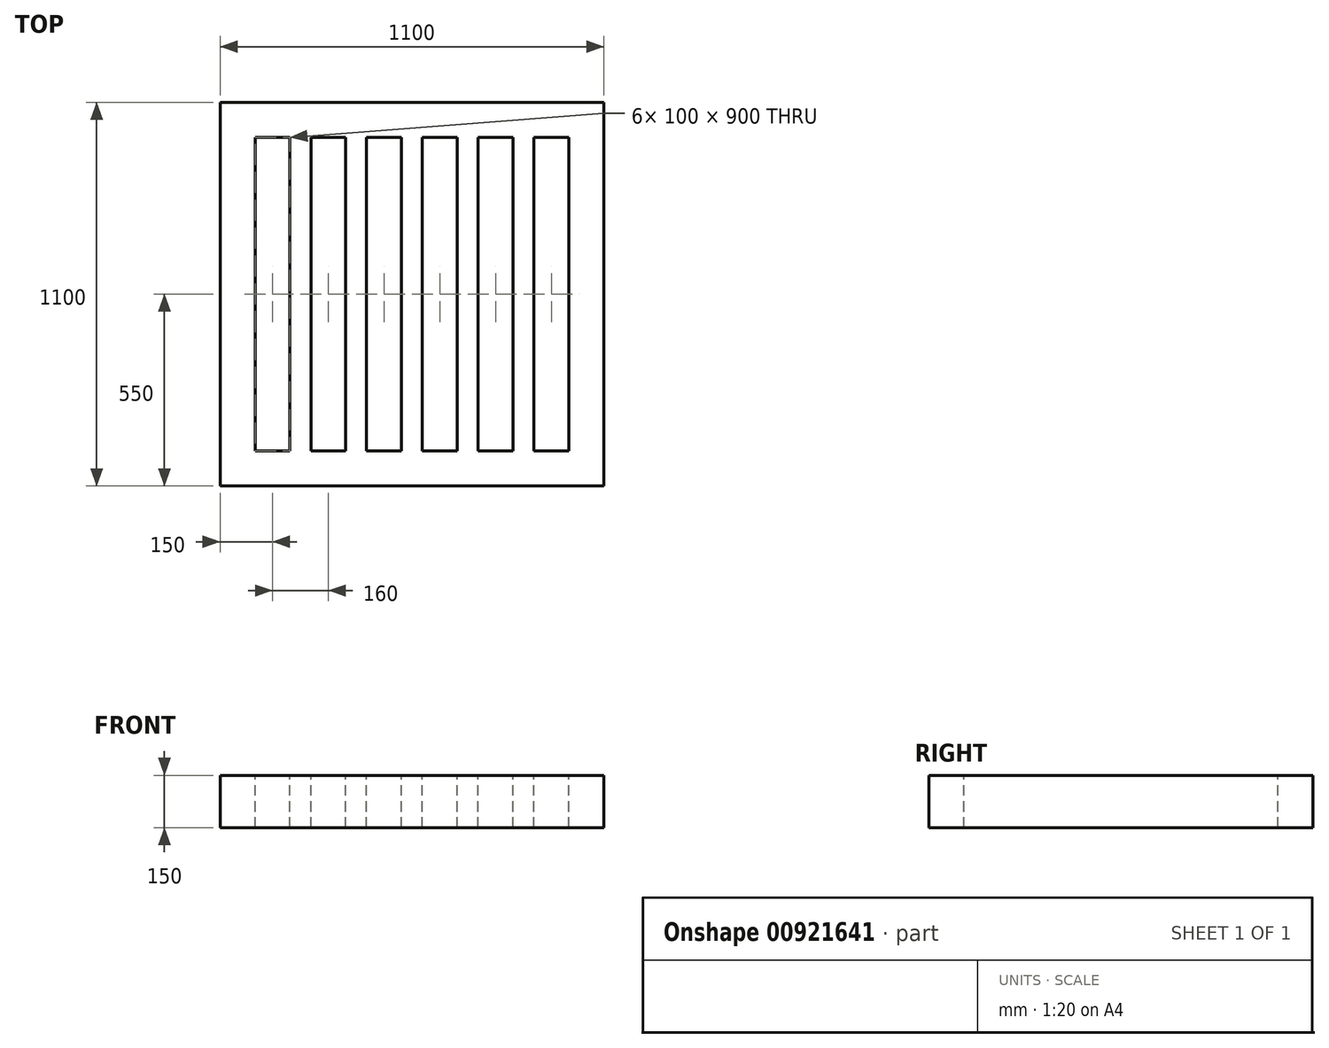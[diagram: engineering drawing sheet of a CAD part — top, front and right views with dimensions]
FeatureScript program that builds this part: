
annotation { "Feature Type Name" : "Feature", "Feature Type Description" : "" }
export const myFeature = defineFeature(function(context is Context, id is Id, definition is map)
    precondition{}
    {
        {
            var Q0;
            Q0=qCreatedBy(makeId("Top.planeOp"),FACE);
            var sketch = newSketch(context, id + "F0", { "sketchPlane" : qUnion([Q0])});
            skLineSegment(sketch, "E0.bottom", {"start": v(550, 550) * mm, "end": v(-550, 550) * mm});
            skLineSegment(sketch, "E0.top", {"start": v(550, -550) * mm, "end": v(-550, -550) * mm});
            skLineSegment(sketch, "E0.left", {"start": v(550, 550) * mm, "end": v(550, -550) * mm});
            skLineSegment(sketch, "E0.right", {"start": v(-550, 550) * mm, "end": v(-550, -550) * mm});
            skPoint(sketch, "E0.middle", {"position": v(0, 0) * mm});
            skSolve(sketch);
        }
        {
            var Q0;
            Q0=makeQuery(id+"F0.imprint","IMPRINT",FACE,{"disambiguationData":[TD([[makeQuery(id+"F0.imprint","IMPRINT",EDGE,{"derivedFrom":sQuery(id+"F0.wireOp",EDGE,"E0.bottom")}),1.0]])]});
            extrude(context, id + "F1", {"entities" : qUnion([Q0]), "depth" : 150 * mm, "offsetDistance" : 25 * mm});
        }
        {
            var Q0;
            Q0=makeQuery(id+"F1.opExtrude","CAP_FACE",FACE,{"disambiguationData":[OSD([sQuery(id+"F0.wireOp",EDGE,"E0.bottom"),sQuery(id+"F0.wireOp",EDGE,"E0.top"),sQuery(id+"F0.wireOp",EDGE,"E0.left"),sQuery(id+"F0.wireOp",EDGE,"E0.right")])],"isStart":false});
            var sketch = newSketch(context, id + "F2", { "sketchPlane" : qUnion([Q0])});
            skLineSegment(sketch, "E1.bottom", {"start": v(-450, 450) * mm, "end": v(-350, 450) * mm});
            skLineSegment(sketch, "E1.top", {"start": v(-450, -450) * mm, "end": v(-350, -450) * mm});
            skLineSegment(sketch, "E1.left", {"start": v(-450, 450) * mm, "end": v(-450, -450) * mm});
            skLineSegment(sketch, "E1.right", {"start": v(-350, 450) * mm, "end": v(-350, -450) * mm});
            skLineSegment(sketch, "E2.1.0.0", {"start": v(-290, 450) * mm, "end": v(-190, 450) * mm});
            skLineSegment(sketch, "E2.1.0.1", {"start": v(-190, 450) * mm, "end": v(-190, -450) * mm});
            skLineSegment(sketch, "E2.1.0.2", {"start": v(-290, 450) * mm, "end": v(-290, -450) * mm});
            skLineSegment(sketch, "E2.1.0.3", {"start": v(-290, -450) * mm, "end": v(-190, -450) * mm});
            skLineSegment(sketch, "E2.2.0.0", {"start": v(-130, 450) * mm, "end": v(-30, 450) * mm});
            skLineSegment(sketch, "E2.2.0.1", {"start": v(-30, 450) * mm, "end": v(-30, -450) * mm});
            skLineSegment(sketch, "E2.2.0.2", {"start": v(-130, 450) * mm, "end": v(-130, -450) * mm});
            skLineSegment(sketch, "E2.2.0.3", {"start": v(-130, -450) * mm, "end": v(-30, -450) * mm});
            skLineSegment(sketch, "E2.3.0.0", {"start": v(30, 450) * mm, "end": v(130, 450) * mm});
            skLineSegment(sketch, "E2.3.0.1", {"start": v(130, 450) * mm, "end": v(130, -450) * mm});
            skLineSegment(sketch, "E2.3.0.2", {"start": v(30, 450) * mm, "end": v(30, -450) * mm});
            skLineSegment(sketch, "E2.3.0.3", {"start": v(30, -450) * mm, "end": v(130, -450) * mm});
            skLineSegment(sketch, "E2.4.0.0", {"start": v(190, 450) * mm, "end": v(290, 450) * mm});
            skLineSegment(sketch, "E2.4.0.1", {"start": v(290, 450) * mm, "end": v(290, -450) * mm});
            skLineSegment(sketch, "E2.4.0.2", {"start": v(190, 450) * mm, "end": v(190, -450) * mm});
            skLineSegment(sketch, "E2.4.0.3", {"start": v(190, -450) * mm, "end": v(290, -450) * mm});
            skLineSegment(sketch, "E2.5.0.0", {"start": v(350, 450) * mm, "end": v(450, 450) * mm});
            skLineSegment(sketch, "E2.5.0.1", {"start": v(450, 450) * mm, "end": v(450, -450) * mm});
            skLineSegment(sketch, "E2.5.0.2", {"start": v(350, 450) * mm, "end": v(350, -450) * mm});
            skLineSegment(sketch, "E2.5.0.3", {"start": v(350, -450) * mm, "end": v(450, -450) * mm});
            skLineSegment(sketch, "E2.direction1", {"start": v(-450, 450) * mm, "end": v(-290, 450) * mm, "construction": true});
            skSolve(sketch);
        }
        {
            var Q0;
            Q0=makeQuery(id+"F2.imprint","IMPRINT",FACE,{"disambiguationData":[TD([[makeQuery(id+"F2.imprint","IMPRINT",EDGE,{"derivedFrom":sQuery(id+"F2.wireOp",EDGE,"E1.bottom")}),-1.0]])]});
            var Q1;
            Q1=makeQuery(id+"F2.imprint","IMPRINT",FACE,{"disambiguationData":[TD([[makeQuery(id+"F2.imprint","IMPRINT",EDGE,{"derivedFrom":sQuery(id+"F2.wireOp",EDGE,"E2.1.0.0")}),-1.0]])]});
            var Q2;
            Q2=makeQuery(id+"F2.imprint","IMPRINT",FACE,{"disambiguationData":[TD([[makeQuery(id+"F2.imprint","IMPRINT",EDGE,{"derivedFrom":sQuery(id+"F2.wireOp",EDGE,"E2.2.0.0")}),-1.0]])]});
            var Q3;
            Q3=makeQuery(id+"F2.imprint","IMPRINT",FACE,{"disambiguationData":[TD([[makeQuery(id+"F2.imprint","IMPRINT",EDGE,{"derivedFrom":sQuery(id+"F2.wireOp",EDGE,"E2.3.0.0")}),-1.0]])]});
            var Q4;
            Q4=makeQuery(id+"F2.imprint","IMPRINT",FACE,{"disambiguationData":[TD([[makeQuery(id+"F2.imprint","IMPRINT",EDGE,{"derivedFrom":sQuery(id+"F2.wireOp",EDGE,"E2.4.0.0")}),-1.0]])]});
            var Q5;
            Q5=makeQuery(id+"F2.imprint","IMPRINT",FACE,{"disambiguationData":[TD([[makeQuery(id+"F2.imprint","IMPRINT",EDGE,{"derivedFrom":sQuery(id+"F2.wireOp",EDGE,"E2.5.0.0")}),-1.0]])]});
            extrude(context, id + "F3", {"entities" : qUnion([Q0, Q1, Q2, Q3, Q4, Q5]), "operationType" : NewBodyOperationType.REMOVE, "oppositeDirection" : true, "depth" : 150 * mm, "offsetDistance" : 25 * mm});
        }
    });
